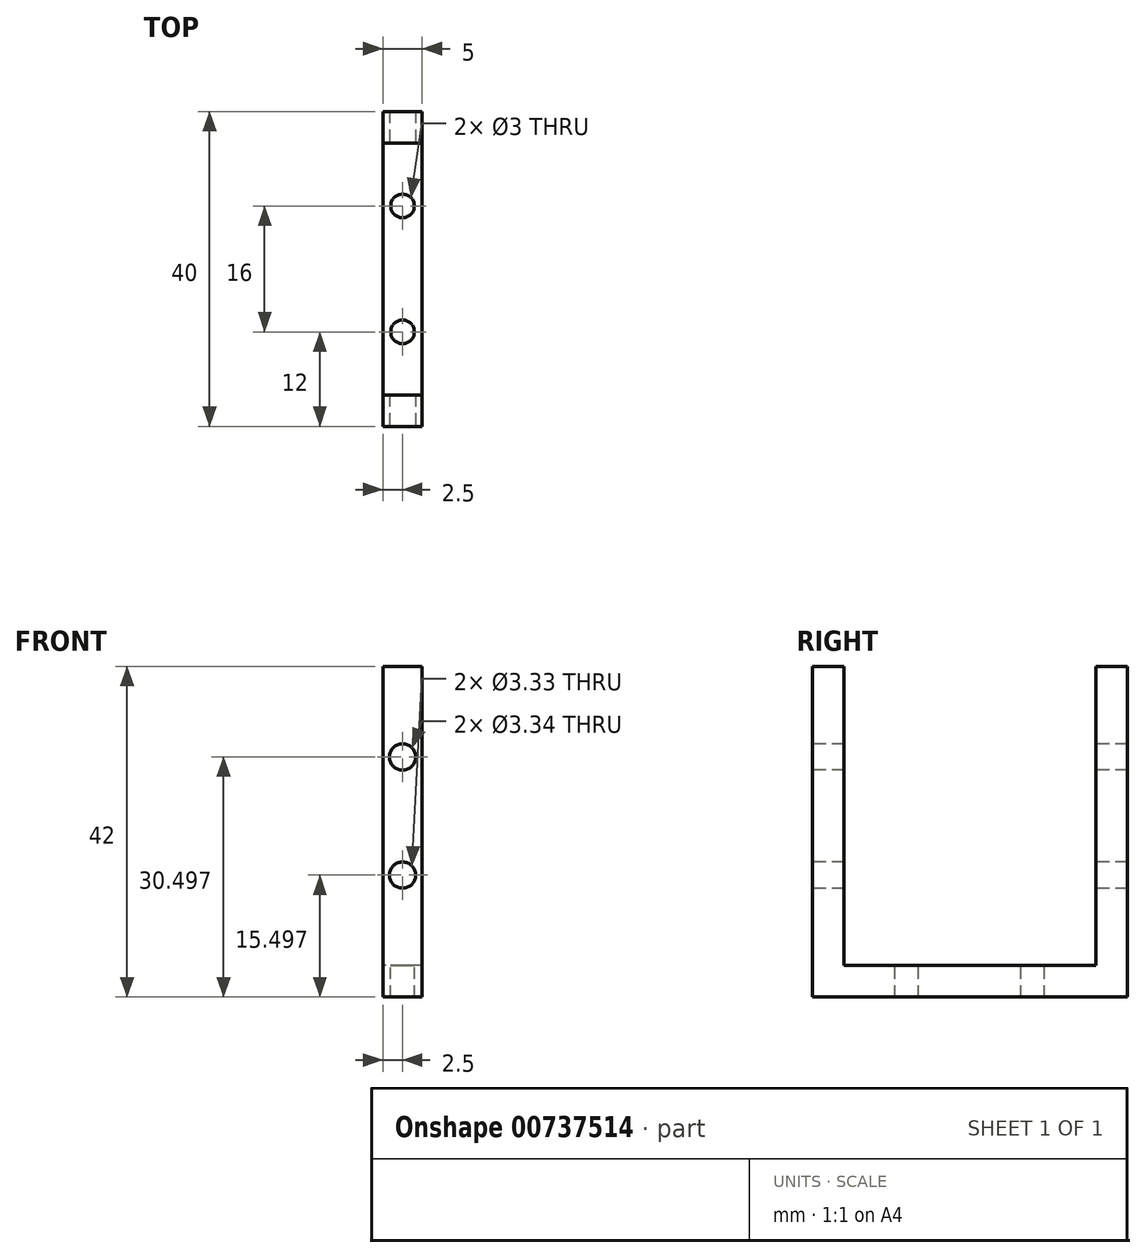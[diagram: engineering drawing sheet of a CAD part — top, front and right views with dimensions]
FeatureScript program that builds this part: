
annotation { "Feature Type Name" : "Feature", "Feature Type Description" : "" }
export const myFeature = defineFeature(function(context is Context, id is Id, definition is map)
    precondition{}
    {
        {
            var Q0;
            Q0=qCreatedBy(makeId("Right.planeOp"),FACE);
            var sketch = newSketch(context, id + "F0", { "sketchPlane" : qUnion([Q0])});
            skLineSegment(sketch, "E0", {"start": v(0, -8.88) * mm, "end": v(-16, -8.88) * mm});
            skLineSegment(sketch, "E1", {"start": v(-16, -8.88) * mm, "end": v(-16, 29.12) * mm});
            skLineSegment(sketch, "E2", {"start": v(-16, 29.12) * mm, "end": v(-20, 29.12) * mm});
            skLineSegment(sketch, "E3", {"start": v(-20, 29.12) * mm, "end": v(-20, -12.88) * mm});
            skLineSegment(sketch, "E4", {"start": v(-20, -12.88) * mm, "end": v(0, -12.88) * mm});
            skLineSegment(sketch, "E5.MirrorCS", {"start": v(0, -8.88) * mm, "end": v(16, -8.88) * mm});
            skLineSegment(sketch, "E6.MirrorCS", {"start": v(20, -12.88) * mm, "end": v(0, -12.88) * mm});
            skLineSegment(sketch, "E7.MirrorCS", {"start": v(20, 29.12) * mm, "end": v(20, -12.88) * mm});
            skLineSegment(sketch, "E8.MirrorCS", {"start": v(16, -8.88) * mm, "end": v(16, 29.12) * mm});
            skLineSegment(sketch, "E9.MirrorCS", {"start": v(16, 29.12) * mm, "end": v(20, 29.12) * mm});
            skSolve(sketch);
        }
        {
            var Q0;
            Q0=makeQuery(id+"F0.imprint","IMPRINT",FACE,{"disambiguationData":[TD([[makeQuery(id+"F0.imprint","IMPRINT",EDGE,{"derivedFrom":sQuery(id+"F0.wireOp",EDGE,"E0")}),1.0]])]});
            extrude(context, id + "F1", {"entities" : qUnion([Q0]), "depth" : 5 * mm, "offsetDistance" : 25 * mm});
        }
        {
            var Q0;
            Q0=makeQuery(id+"F1.opExtrude","SWEPT_FACE",FACE,{"disambiguationData":[OSD([sQuery(id+"F0.wireOp",EDGE,"E3")])]});
            var sketch = newSketch(context, id + "F2", { "sketchPlane" : qUnion([Q0])});
            skCircle(sketch, "E10", {"center": v(2.5, 17.62) * mm, "radius": 1.67 * mm});
            skPoint(sketch, "E10.centerSnap0", {"position": v(2.5, 29.12) * mm});
            skCircle(sketch, "E11", {"center": v(2.5, 2.62) * mm, "radius": 1.67 * mm});
            skSolve(sketch);
        }
        {
            var Q0;
            Q0 = qSketchRegion(id + "F2", true);
            extrude(context, id + "F3", {"entities" : qUnion([Q0]), "operationType" : NewBodyOperationType.REMOVE, "endBound" : BoundingType.THROUGH_ALL, "oppositeDirection" : true, "depth" : 25 * mm, "offsetDistance" : 25 * mm});
        }
        {
            var Q0;
            Q0=makeQuery(id+"F1.opExtrude","SWEPT_FACE",FACE,{"disambiguationData":[OSD([sQuery(id+"F0.wireOp",EDGE,"E0"),sQuery(id+"F0.wireOp",EDGE,"E5.MirrorCS")])]});
            var sketch = newSketch(context, id + "F4", { "sketchPlane" : qUnion([Q0])});
            skCircle(sketch, "E12", {"center": v(2.5, -8) * mm, "radius": 1.5 * mm});
            skPoint(sketch, "E12.centerSnap0", {"position": v(2.5, -16) * mm});
            skCircle(sketch, "E13", {"center": v(2.5, 8) * mm, "radius": 1.5 * mm});
            skPoint(sketch, "E13.centerSnap0", {"position": v(2.5, 16) * mm});
            skSolve(sketch);
        }
        {
            var Q0;
            Q0 = qSketchRegion(id + "F4", true);
            extrude(context, id + "F5", {"entities" : qUnion([Q0]), "operationType" : NewBodyOperationType.REMOVE, "endBound" : BoundingType.THROUGH_ALL, "oppositeDirection" : true, "depth" : 25 * mm, "offsetDistance" : 25 * mm});
        }
    });
